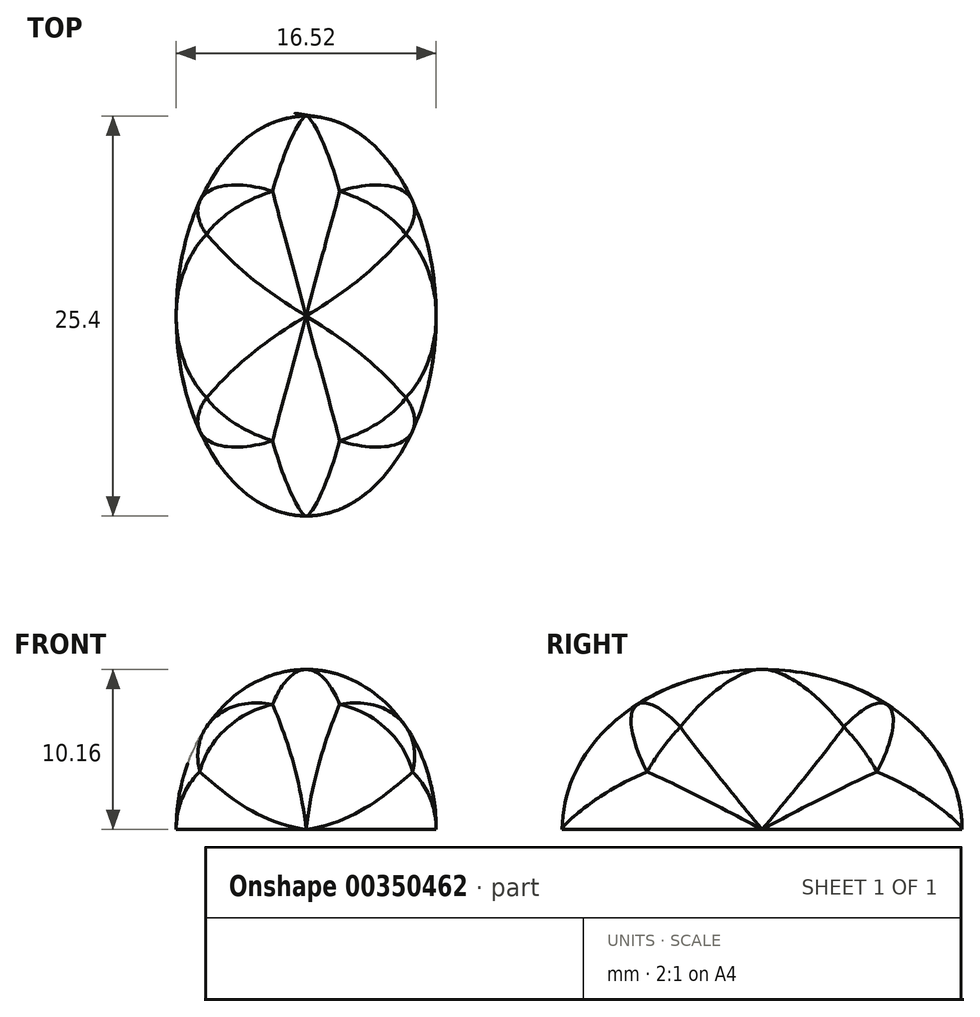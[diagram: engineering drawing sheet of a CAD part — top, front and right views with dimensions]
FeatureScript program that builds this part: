
annotation { "Feature Type Name" : "Feature", "Feature Type Description" : "" }
export const myFeature = defineFeature(function(context is Context, id is Id, definition is map)
    precondition{}
    {
        {
            var Q0;
            Q0=qCreatedBy(makeId("Top.planeOp"),FACE);
            var sketch = newSketch(context, id + "F0", { "sketchPlane" : qUnion([Q0])});
            skEllipse(sketch, "E0", {"center": v(0, 0) * mm, "majorRadius": 12.7 * mm, "minorRadius": 8.26 * mm, "majorAxis": v(0, 1)});
            skSolve(sketch);
        }
        {
            var Q0;
            Q0=makeQuery(id+"F0.imprint","IMPRINT",FACE,{"disambiguationData":[TD([[makeQuery(id+"F0.imprint","IMPRINT",EDGE,{"derivedFrom":sQuery(id+"F0.wireOp",EDGE,"E0")}),1.0]])]});
            extrude(context, id + "F1", {"entities" : qUnion([Q0]), "depth" : 10.16 * mm});
        }
        {
            var Q0;
            Q0=qCreatedBy(makeId("Front.planeOp"),FACE);
            var sketch = newSketch(context, id + "F2", { "sketchPlane" : qUnion([Q0])});
            skEllipticalArc(sketch, "E1", {});
            skLineSegment(sketch, "E2", {"start": v(8.26, 0) * mm, "end": v(8.26, 12.35) * mm});
            skLineSegment(sketch, "E3", {"start": v(-8.26, 0) * mm, "end": v(-8.26, 12.73) * mm});
            skLineSegment(sketch, "E4", {"start": v(-8.26, 12.73) * mm, "end": v(8.26, 12.35) * mm});
            const initialGuessF2  = {"E1": [0, 0, 0, 1, 0.01016, 0.008255, 4.71238898038469, 1.5707963267948966]};
            skSetInitialGuess(sketch, initialGuessF2);
            skSolve(sketch);
        }
        {
            var Q0;
            Q0 = qSketchRegion(id + "F2", true);
            extrude(context, id + "F3", {"entities" : qUnion([Q0]), "operationType" : NewBodyOperationType.REMOVE, "endBound" : BoundingType.SYMMETRIC, "oppositeDirection" : true, "depth" : 25.4 * mm});
        }
        {
            var Q0;
            Q0=qCreatedBy(makeId("Right.planeOp"),FACE);
            var sketch = newSketch(context, id + "F4", { "sketchPlane" : qUnion([Q0])});
            skEllipticalArc(sketch, "E5", {});
            skLineSegment(sketch, "E6", {"start": v(12.7, 0) * mm, "end": v(12.7, 13.18) * mm});
            skLineSegment(sketch, "E7", {"start": v(-12.7, 0) * mm, "end": v(-12.7, 12.71) * mm});
            skLineSegment(sketch, "E8", {"start": v(-12.7, 12.71) * mm, "end": v(12.7, 13.18) * mm});
            const initialGuessF4  = {"E5": [0, 0, 0, 1, 0.01016, 0.0127, 4.71238898038469, 1.5707963267948966]};
            skSetInitialGuess(sketch, initialGuessF4);
            skSolve(sketch);
        }
        {
            var Q0;
            Q0=makeQuery(id+"F4.imprint","IMPRINT",FACE,{"disambiguationData":[TD([[makeQuery(id+"F4.imprint","IMPRINT",EDGE,{"derivedFrom":sQuery(id+"F4.wireOp",EDGE,"E5")}),-1.0]])]});
            extrude(context, id + "F5", {"entities" : qUnion([Q0]), "operationType" : NewBodyOperationType.REMOVE, "endBound" : BoundingType.SYMMETRIC, "oppositeDirection" : true, "depth" : 25.4 * mm});
        }
        {
            var Q0;
            Q0=makeQuery(id+"F5.boolean.opBoolean","INTERSECT",EDGE,{"disambiguationData":[OD(0.0)],"derivedFrom":[makeQuery(id+"F3.boolean.opBoolean","SPLIT",FACE,{"disambiguationData":[OD(0.0)],"derivedFrom":makeQuery(id+"F1.opExtrude","SWEPT_FACE",FACE,{"disambiguationData":[OSD([sQuery(id+"F0.wireOp",EDGE,"E0")])]})}),makeQuery(id+"F5.opExtrude","SWEPT_FACE",FACE,{"disambiguationData":[OSD([sQuery(id+"F4.wireOp",EDGE,"E5")])]})]});
            var Q1;
            Q1=makeQuery(id+"F5.boolean.opBoolean","SPLIT",EDGE,{"disambiguationData":[OD(0.0)],"derivedFrom":makeQuery(id+"F3.boolean.opBoolean","INTERSECT",EDGE,{"disambiguationData":[OD(0.0)],"derivedFrom":[makeQuery(id+"F1.opExtrude","SWEPT_FACE",FACE,{"disambiguationData":[OSD([sQuery(id+"F0.wireOp",EDGE,"E0")])]}),makeQuery(id+"F3.opExtrude","SWEPT_FACE",FACE,{"disambiguationData":[OSD([sQuery(id+"F2.wireOp",EDGE,"E1")])]})]})});
            var Q2;
            Q2=makeQuery(id+"F5.boolean.opBoolean","INTERSECT",EDGE,{"disambiguationData":[OD(0.0)],"derivedFrom":[makeQuery(id+"F3.boolean.opBoolean","COPY",FACE,{"derivedFrom":makeQuery(id+"F3.opExtrude","SWEPT_FACE",FACE,{"disambiguationData":[OSD([sQuery(id+"F2.wireOp",EDGE,"E1")])]})}),makeQuery(id+"F5.opExtrude","SWEPT_FACE",FACE,{"disambiguationData":[OSD([sQuery(id+"F4.wireOp",EDGE,"E5")])]})]});
            fillet(context, id + "F6", {"entities" : qUnion([Q0, Q1, Q2]), "radius" : 5.08 * mm, "tangentPropagation" : true, "allowEdgeOverflow" : false});
        }
        {
            var Q0;
            Q0=makeQuery(id+"F5.boolean.opBoolean","INTERSECT",EDGE,{"disambiguationData":[OD(0.0)],"derivedFrom":[makeQuery(id+"F3.boolean.opBoolean","SPLIT",FACE,{"disambiguationData":[OD(1.0)],"derivedFrom":makeQuery(id+"F1.opExtrude","SWEPT_FACE",FACE,{"disambiguationData":[OSD([sQuery(id+"F0.wireOp",EDGE,"E0")])]})}),makeQuery(id+"F5.opExtrude","SWEPT_FACE",FACE,{"disambiguationData":[OSD([sQuery(id+"F4.wireOp",EDGE,"E5")])]})]});
            var Q1;
            Q1=makeQuery(id+"F5.boolean.opBoolean","INTERSECT",EDGE,{"disambiguationData":[OD(2.0)],"derivedFrom":[makeQuery(id+"F3.boolean.opBoolean","COPY",FACE,{"derivedFrom":makeQuery(id+"F3.opExtrude","SWEPT_FACE",FACE,{"disambiguationData":[OSD([sQuery(id+"F2.wireOp",EDGE,"E1")])]})}),makeQuery(id+"F5.opExtrude","SWEPT_FACE",FACE,{"disambiguationData":[OSD([sQuery(id+"F4.wireOp",EDGE,"E5")])]})]});
            var Q2;
            Q2=makeQuery(id+"F5.boolean.opBoolean","SPLIT",EDGE,{"disambiguationData":[OD(0.0)],"derivedFrom":makeQuery(id+"F3.boolean.opBoolean","INTERSECT",EDGE,{"disambiguationData":[OD(1.0)],"derivedFrom":[makeQuery(id+"F1.opExtrude","SWEPT_FACE",FACE,{"disambiguationData":[OSD([sQuery(id+"F0.wireOp",EDGE,"E0")])]}),makeQuery(id+"F3.opExtrude","SWEPT_FACE",FACE,{"disambiguationData":[OSD([sQuery(id+"F2.wireOp",EDGE,"E1")])]})]})});
            fillet(context, id + "F7", {"entities" : qUnion([Q0, Q1, Q2]), "radius" : 5.08 * mm, "tangentPropagation" : true, "allowEdgeOverflow" : false});
        }
        {
            var Q0;
            Q0=makeQuery(id+"F5.boolean.opBoolean","INTERSECT",EDGE,{"disambiguationData":[OD(3.0)],"derivedFrom":[makeQuery(id+"F3.boolean.opBoolean","COPY",FACE,{"derivedFrom":makeQuery(id+"F3.opExtrude","SWEPT_FACE",FACE,{"disambiguationData":[OSD([sQuery(id+"F2.wireOp",EDGE,"E1")])]})}),makeQuery(id+"F5.opExtrude","SWEPT_FACE",FACE,{"disambiguationData":[OSD([sQuery(id+"F4.wireOp",EDGE,"E5")])]})]});
            var Q1;
            Q1=makeQuery(id+"F5.boolean.opBoolean","SPLIT",EDGE,{"disambiguationData":[OD(1.0)],"derivedFrom":makeQuery(id+"F3.boolean.opBoolean","INTERSECT",EDGE,{"disambiguationData":[OD(1.0)],"derivedFrom":[makeQuery(id+"F1.opExtrude","SWEPT_FACE",FACE,{"disambiguationData":[OSD([sQuery(id+"F0.wireOp",EDGE,"E0")])]}),makeQuery(id+"F3.opExtrude","SWEPT_FACE",FACE,{"disambiguationData":[OSD([sQuery(id+"F2.wireOp",EDGE,"E1")])]})]})});
            var Q2;
            Q2=makeQuery(id+"F5.boolean.opBoolean","INTERSECT",EDGE,{"disambiguationData":[OD(1.0)],"derivedFrom":[makeQuery(id+"F3.boolean.opBoolean","SPLIT",FACE,{"disambiguationData":[OD(1.0)],"derivedFrom":makeQuery(id+"F1.opExtrude","SWEPT_FACE",FACE,{"disambiguationData":[OSD([sQuery(id+"F0.wireOp",EDGE,"E0")])]})}),makeQuery(id+"F5.opExtrude","SWEPT_FACE",FACE,{"disambiguationData":[OSD([sQuery(id+"F4.wireOp",EDGE,"E5")])]})]});
            fillet(context, id + "F8", {"entities" : qUnion([Q0, Q1, Q2]), "radius" : 5.08 * mm, "tangentPropagation" : true, "allowEdgeOverflow" : false});
        }
        {
            var Q0;
            Q0=makeQuery(id+"F5.boolean.opBoolean","INTERSECT",EDGE,{"disambiguationData":[OD(1.0)],"derivedFrom":[makeQuery(id+"F3.boolean.opBoolean","SPLIT",FACE,{"disambiguationData":[OD(0.0)],"derivedFrom":makeQuery(id+"F1.opExtrude","SWEPT_FACE",FACE,{"disambiguationData":[OSD([sQuery(id+"F0.wireOp",EDGE,"E0")])]})}),makeQuery(id+"F5.opExtrude","SWEPT_FACE",FACE,{"disambiguationData":[OSD([sQuery(id+"F4.wireOp",EDGE,"E5")])]})]});
            var Q1;
            Q1=makeQuery(id+"F5.boolean.opBoolean","INTERSECT",EDGE,{"disambiguationData":[OD(1.0)],"derivedFrom":[makeQuery(id+"F3.boolean.opBoolean","COPY",FACE,{"derivedFrom":makeQuery(id+"F3.opExtrude","SWEPT_FACE",FACE,{"disambiguationData":[OSD([sQuery(id+"F2.wireOp",EDGE,"E1")])]})}),makeQuery(id+"F5.opExtrude","SWEPT_FACE",FACE,{"disambiguationData":[OSD([sQuery(id+"F4.wireOp",EDGE,"E5")])]})]});
            var Q2;
            Q2=makeQuery(id+"F5.boolean.opBoolean","SPLIT",EDGE,{"disambiguationData":[OD(1.0)],"derivedFrom":makeQuery(id+"F3.boolean.opBoolean","INTERSECT",EDGE,{"disambiguationData":[OD(0.0)],"derivedFrom":[makeQuery(id+"F1.opExtrude","SWEPT_FACE",FACE,{"disambiguationData":[OSD([sQuery(id+"F0.wireOp",EDGE,"E0")])]}),makeQuery(id+"F3.opExtrude","SWEPT_FACE",FACE,{"disambiguationData":[OSD([sQuery(id+"F2.wireOp",EDGE,"E1")])]})]})});
            fillet(context, id + "F9", {"entities" : qUnion([Q0, Q1, Q2]), "radius" : 5.08 * mm, "tangentPropagation" : true, "allowEdgeOverflow" : false});
        }
    });
